# Revit family: Mount_RigidRail_Kattsafe_Side
name_source: partatom
category: Specialty Equipment
units: mm (PartAtom-declared; Revit-internal decimal feet)

## family parameters
Always vertical = Yes
Cut with Voids When Loaded = No
Enable Cutting in Views = No
Maintain Annotation Orientation = No
OmniClass Number = 23.27.71.21
Part Type = Normal
Room Calculation Point = No
Round Connector Dimension = Use Diameter
Shared = No
Work Plane-Based = No

## types (2) — shared parameters
Assembly Code = E1090100
Description = Rigid rails provide significant spanning capabilities, making them very versatile where there are limited support structures. The high strength aluminium construction, along with the unique t-bolt assembly makes it a very simple and easily adaptable system to install.
Export Type to IFC As = IfcBuildingElementProxy
IfcExportAs = IfcBuildingElementProxy
IfcExportType = USERDEFINED
Manufacturer = Kattsafe®
ManufacturerOverallWidth = 100 mm  [stored 0.328084 ft]
ManufacturerURLProductSpecific = https://kattsafe.com.au
ModifiedIssue = 20240430 $
Type IFC Predefined Type = USERDEFINED
URL = https://kattsafe.com.au
Uniclass2015Code = Pr_20_85_09
Uniclass2015Title = Brackets
Uniclass2015Version = Products v1.23
zero-valued in all types: Default Elevation

## per-type parameters (varying)
| type | 100Bracket | 200Bracket | ManufacturerOverallDepth | ManufacturerOverallHeight | ManufacturerSpecCode | Model | OuterRadiusCalc | Thickness | Type Comments |
| 200mm Bracket (OH266.200) | No | Yes | 230 mm | 300 mm  [stored 0.984252 ft] | OH266.200 | OH266.200 | 12 mm  [stored 0.0393701 ft] | 6 mm  [stored 0.019685 ft] | Side Mount Bracket - 200mm |
| 100mm Bracket (OH266.100) | Yes | No | 105 mm | 105 mm | OH266.100 | OH266.100 | 20 mm  [stored 0.0656168 ft] | 10 mm  [stored 0.0328084 ft] | Side Mount Bracket - 100mm |

note: [stored X ft] marks values corroborated as IEEE doubles in the binary element streams (Revit-internal decimal feet)

## geometry (parser evidence)
native form markers: Sweep x1
no freeform markers — native parametric forms only
